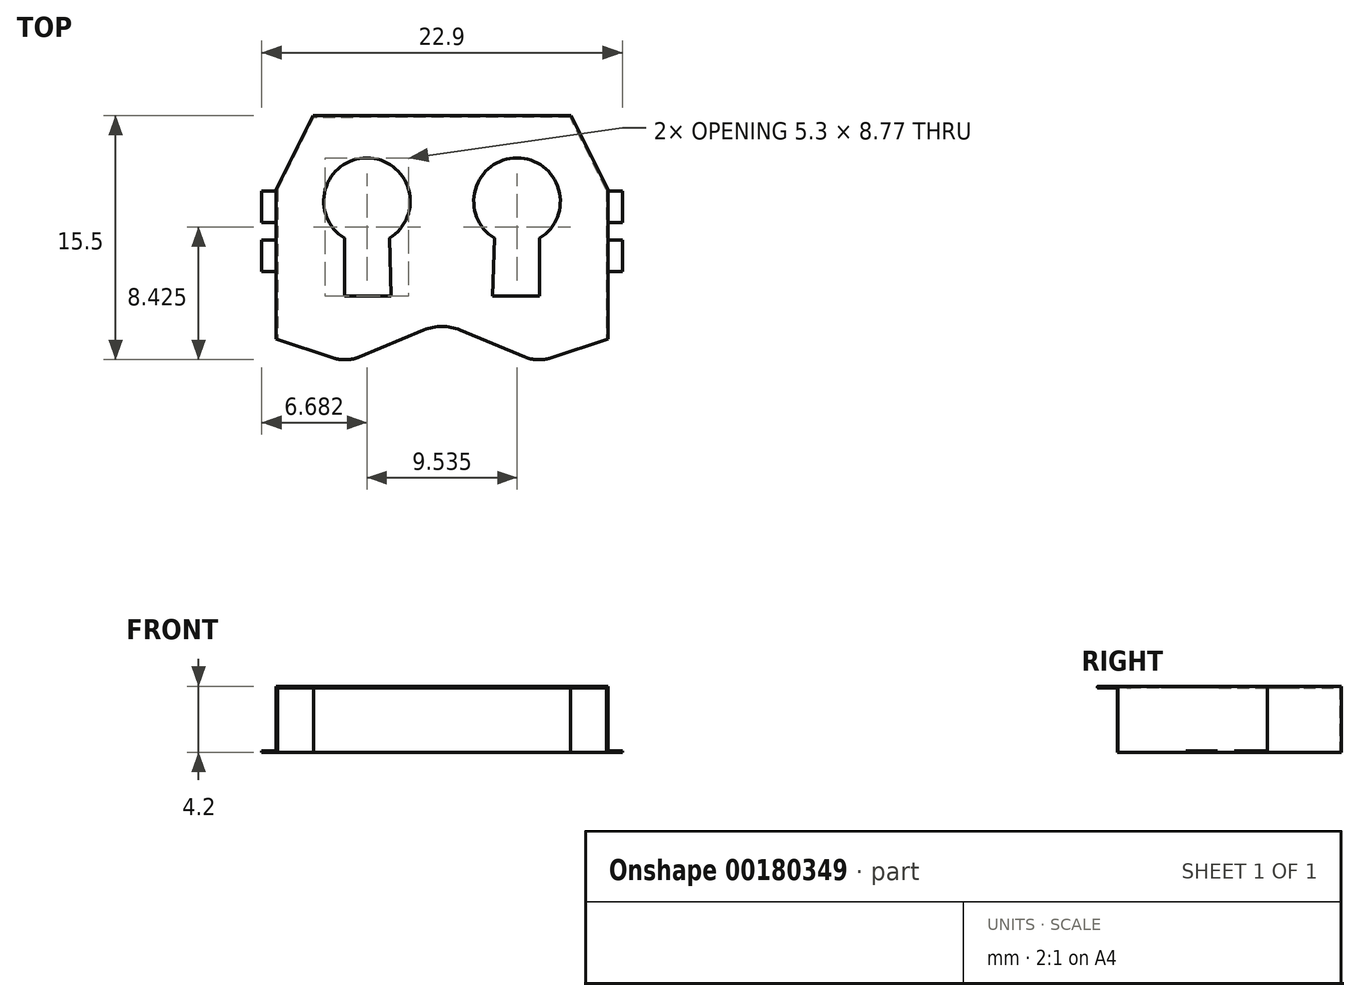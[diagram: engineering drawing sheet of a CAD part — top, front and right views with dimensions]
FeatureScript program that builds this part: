
annotation { "Feature Type Name" : "Feature", "Feature Type Description" : "" }
export const myFeature = defineFeature(function(context is Context, id is Id, definition is map)
    precondition{}
    {
        {
            var Q0;
            Q0=qCreatedBy(makeId("Top.planeOp"),FACE);
            var sketch = newSketch(context, id + "F0", { "sketchPlane" : qUnion([Q0])});
            skLineSegment(sketch, "E0", {"start": v(-8.2, 10.06) * mm, "end": v(-10.55, 5.35) * mm});
            skLineSegment(sketch, "E1", {"start": v(-10.55, -4.15) * mm, "end": v(-6.9, -5.34) * mm});
            skLineSegment(sketch, "E2", {"start": v(-10.55, 5.35) * mm, "end": v(-10.55, -4.15) * mm});
            skLineSegment(sketch, "E3", {"start": v(-8.2, 10.06) * mm, "end": v(0, 10.06) * mm});
            skLineSegment(sketch, "E4", {"start": v(-6.28, -5.44) * mm, "end": v(-6.05, -5.44) * mm});
            skLineSegment(sketch, "E5", {"start": v(-5.28, -5.29) * mm, "end": v(-1.16, -3.57) * mm});
            skLineSegment(sketch, "E6.MirrorCS", {"start": v(6.28, -5.44) * mm, "end": v(6.05, -5.44) * mm});
            skLineSegment(sketch, "E7.MirrorCS", {"start": v(8.2, 10.06) * mm, "end": v(0, 10.06) * mm});
            skLineSegment(sketch, "E8.MirrorCS", {"start": v(5.28, -5.29) * mm, "end": v(1.16, -3.57) * mm});
            skLineSegment(sketch, "E9.MirrorCS", {"start": v(10.55, -4.15) * mm, "end": v(6.9, -5.34) * mm});
            skLineSegment(sketch, "E10.MirrorCS", {"start": v(10.55, 5.35) * mm, "end": v(10.55, -4.15) * mm});
            skLineSegment(sketch, "E11.MirrorCS", {"start": v(8.2, 10.06) * mm, "end": v(10.55, 5.35) * mm});
            skPoint(sketch, "E12.visualSharp", {"position": v(0, -3.09) * mm});
            skArc(sketch, "E12.filletArc", {"start": v(1.16, -3.57) * mm, "mid": v(0, -3.34) * mm, "end": v(-1.16, -3.57) * mm});
            skPoint(sketch, "E13.visualSharp", {"position": v(-6.6, -5.44) * mm});
            skArc(sketch, "E13.filletArc", {"start": v(-6.9, -5.34) * mm, "mid": v(-6.59, -5.42) * mm, "end": v(-6.28, -5.44) * mm});
            skPoint(sketch, "E14.visualSharp", {"position": v(-5.65, -5.44) * mm});
            skArc(sketch, "E14.filletArc", {"start": v(-6.05, -5.44) * mm, "mid": v(-5.65, -5.4) * mm, "end": v(-5.28, -5.29) * mm});
            skPoint(sketch, "E15.visualSharp", {"position": v(5.65, -5.44) * mm});
            skArc(sketch, "E15.filletArc", {"start": v(5.28, -5.29) * mm, "mid": v(5.65, -5.4) * mm, "end": v(6.05, -5.44) * mm});
            skPoint(sketch, "E16.visualSharp", {"position": v(6.6, -5.44) * mm});
            skArc(sketch, "E16.filletArc", {"start": v(6.28, -5.44) * mm, "mid": v(6.59, -5.42) * mm, "end": v(6.9, -5.34) * mm});
            skSolve(sketch);
        }
        {
            var Q0;
            Q0 = qSketchRegion(id + "F0", true);
            extrude(context, id + "F1", {"entities" : qUnion([Q0]), "depth" : 4.2 * mm});
        }
        {
            var Q0;
            Q0=makeQuery(id+"F1.opExtrude","SWEPT_FACE",FACE,{"disambiguationData":[OSD([sQuery(id+"F0.wireOp",EDGE,"E4")])]});
            var sketch = newSketch(context, id + "F2", { "sketchPlane" : qUnion([Q0])});
            skLineSegment(sketch, "E17.bottom", {"start": v(-10.45, 0) * mm, "end": v(10.45, 0) * mm});
            skLineSegment(sketch, "E17.top", {"start": v(-10.45, 4.1) * mm, "end": v(10.45, 4.1) * mm});
            skLineSegment(sketch, "E17.left", {"start": v(-10.45, 0) * mm, "end": v(-10.45, 4.1) * mm});
            skLineSegment(sketch, "E17.right", {"start": v(10.45, 0) * mm, "end": v(10.45, 4.1) * mm});
            skSolve(sketch);
        }
        {
            var Q0;
            Q0 = qSketchRegion(id + "F2", true);
            extrude(context, id + "F3", {"entities" : qUnion([Q0]), "operationType" : NewBodyOperationType.REMOVE, "oppositeDirection" : true, "depth" : 10 * mm});
        }
        {
            var Q0;
            Q0=makeQuery(id+"F1.opExtrude","CAP_FACE",FACE,{"disambiguationData":[OSD([sQuery(id+"F0.wireOp",EDGE,"E0"),sQuery(id+"F0.wireOp",EDGE,"E1"),sQuery(id+"F0.wireOp",EDGE,"E2"),sQuery(id+"F0.wireOp",EDGE,"E3"),sQuery(id+"F0.wireOp",EDGE,"E4"),sQuery(id+"F0.wireOp",EDGE,"E5"),sQuery(id+"F0.wireOp",EDGE,"E6.MirrorCS"),sQuery(id+"F0.wireOp",EDGE,"E7.MirrorCS"),sQuery(id+"F0.wireOp",EDGE,"E8.MirrorCS"),sQuery(id+"F0.wireOp",EDGE,"E9.MirrorCS"),sQuery(id+"F0.wireOp",EDGE,"E10.MirrorCS"),sQuery(id+"F0.wireOp",EDGE,"E11.MirrorCS"),sQuery(id+"F0.wireOp",EDGE,"E12.filletArc"),sQuery(id+"F0.wireOp",EDGE,"E13.filletArc"),sQuery(id+"F0.wireOp",EDGE,"E14.filletArc"),sQuery(id+"F0.wireOp",EDGE,"E15.filletArc"),sQuery(id+"F0.wireOp",EDGE,"E16.filletArc")])],"isStart":true});
            var sketch = newSketch(context, id + "F4", { "sketchPlane" : qUnion([Q0])});
            skLineSegment(sketch, "E18", {"start": v(-10.45, -4.56) * mm, "end": v(-10.45, -5.35) * mm});
            skLineSegment(sketch, "E19", {"start": v(-10.45, -5.35) * mm, "end": v(-8.16, -9.94) * mm});
            skLineSegment(sketch, "E20", {"start": v(10.45, -4.56) * mm, "end": v(10.45, -5.35) * mm});
            skLineSegment(sketch, "E21", {"start": v(10.45, -5.35) * mm, "end": v(8.15, -9.95) * mm});
            skLineSegment(sketch, "E22", {"start": v(8.15, -9.95) * mm, "end": v(-8.16, -9.94) * mm});
            skLineSegment(sketch, "E23", {"start": v(-10.45, -4.56) * mm, "end": v(10.45, -4.56) * mm});
            skSolve(sketch);
        }
        {
            var Q0;
            Q0 = qSketchRegion(id + "F4", true);
            extrude(context, id + "F5", {"entities" : qUnion([Q0]), "operationType" : NewBodyOperationType.REMOVE, "oppositeDirection" : true, "depth" : 4.1 * mm});
        }
        {
            var Q0;
            Q0=qCreatedBy(makeId("Top.planeOp"),FACE);
            var sketch = newSketch(context, id + "F6", { "sketchPlane" : qUnion([Q0])});
            skLineSegment(sketch, "E24.bottom", {"start": v(-10.55, 5.26) * mm, "end": v(-11.45, 5.26) * mm});
            skLineSegment(sketch, "E24.top", {"start": v(-10.55, 3.26) * mm, "end": v(-11.45, 3.26) * mm});
            skLineSegment(sketch, "E24.left", {"start": v(-10.55, 5.26) * mm, "end": v(-10.55, 3.26) * mm});
            skLineSegment(sketch, "E24.right", {"start": v(-11.45, 5.26) * mm, "end": v(-11.45, 3.26) * mm});
            skLineSegment(sketch, "E25.bottom", {"start": v(-10.55, 2.16) * mm, "end": v(-11.45, 2.16) * mm});
            skLineSegment(sketch, "E25.top", {"start": v(-10.55, 0.16) * mm, "end": v(-11.45, 0.16) * mm});
            skLineSegment(sketch, "E25.left", {"start": v(-10.55, 2.16) * mm, "end": v(-10.55, 0.16) * mm});
            skLineSegment(sketch, "E25.right", {"start": v(-11.45, 2.16) * mm, "end": v(-11.45, 0.16) * mm});
            skLineSegment(sketch, "E26.MirrorCS", {"start": v(11.45, 2.16) * mm, "end": v(11.45, 0.16) * mm});
            skLineSegment(sketch, "E27.MirrorCS", {"start": v(10.55, 2.16) * mm, "end": v(10.55, 0.16) * mm});
            skLineSegment(sketch, "E28.MirrorCS", {"start": v(10.55, 0.16) * mm, "end": v(11.45, 0.16) * mm});
            skLineSegment(sketch, "E29.MirrorCS", {"start": v(10.55, 2.16) * mm, "end": v(11.45, 2.16) * mm});
            skLineSegment(sketch, "E30.MirrorCS", {"start": v(11.45, 5.26) * mm, "end": v(11.45, 3.26) * mm});
            skLineSegment(sketch, "E31.MirrorCS", {"start": v(10.55, 3.26) * mm, "end": v(11.45, 3.26) * mm});
            skLineSegment(sketch, "E32.MirrorCS", {"start": v(10.55, 5.26) * mm, "end": v(10.55, 3.26) * mm});
            skLineSegment(sketch, "E33.MirrorCS", {"start": v(10.55, 5.26) * mm, "end": v(11.45, 5.26) * mm});
            skSolve(sketch);
        }
        {
            var Q0;
            Q0 = qSketchRegion(id + "F6", true);
            extrude(context, id + "F7", {"entities" : qUnion([Q0]), "operationType" : NewBodyOperationType.ADD, "depth" : .1 * mm});
        }
        {
            var Q0;
            Q0=makeQuery(id+"F1.opExtrude","CAP_FACE",FACE,{"disambiguationData":[OSD([sQuery(id+"F0.wireOp",EDGE,"E0"),sQuery(id+"F0.wireOp",EDGE,"E1"),sQuery(id+"F0.wireOp",EDGE,"E2"),sQuery(id+"F0.wireOp",EDGE,"E3"),sQuery(id+"F0.wireOp",EDGE,"E4"),sQuery(id+"F0.wireOp",EDGE,"E5"),sQuery(id+"F0.wireOp",EDGE,"E6.MirrorCS"),sQuery(id+"F0.wireOp",EDGE,"E7.MirrorCS"),sQuery(id+"F0.wireOp",EDGE,"E8.MirrorCS"),sQuery(id+"F0.wireOp",EDGE,"E9.MirrorCS"),sQuery(id+"F0.wireOp",EDGE,"E10.MirrorCS"),sQuery(id+"F0.wireOp",EDGE,"E11.MirrorCS"),sQuery(id+"F0.wireOp",EDGE,"E12.filletArc"),sQuery(id+"F0.wireOp",EDGE,"E13.filletArc"),sQuery(id+"F0.wireOp",EDGE,"E14.filletArc"),sQuery(id+"F0.wireOp",EDGE,"E15.filletArc"),sQuery(id+"F0.wireOp",EDGE,"E16.filletArc")])],"isStart":false});
            var sketch = newSketch(context, id + "F8", { "sketchPlane" : qUnion([Q0])});
            skCircle(sketch, "E34", {"center": v(-4.77, 4.62) * mm, "radius": 2.75 * mm});
            skLineSegment(sketch, "E35", {"start": v(-6.2, 2.27) * mm, "end": v(-6.2, -1.4) * mm});
            skLineSegment(sketch, "E36", {"start": v(-6.2, -1.4) * mm, "end": v(-3.22, -1.4) * mm});
            skLineSegment(sketch, "E37", {"start": v(-3.22, -1.4) * mm, "end": v(-3.34, 2.27) * mm});
            skCircle(sketch, "E38.MirrorC", {"center": v(4.77, 4.62) * mm, "radius": 2.75 * mm});
            skLineSegment(sketch, "E39.MirrorCS", {"start": v(6.2, 2.27) * mm, "end": v(6.2, -1.4) * mm});
            skLineSegment(sketch, "E40.MirrorCS", {"start": v(3.22, -1.4) * mm, "end": v(3.34, 2.27) * mm});
            skLineSegment(sketch, "E41.MirrorCS", {"start": v(6.2, -1.4) * mm, "end": v(3.22, -1.4) * mm});
            skSolve(sketch);
        }
        {
            var Q0;
            Q0 = qSketchRegion(id + "F8", true);
            extrude(context, id + "F9", {"entities" : qUnion([Q0]), "operationType" : NewBodyOperationType.REMOVE, "oppositeDirection" : true, "depth" : 25 * mm});
        }
    });
